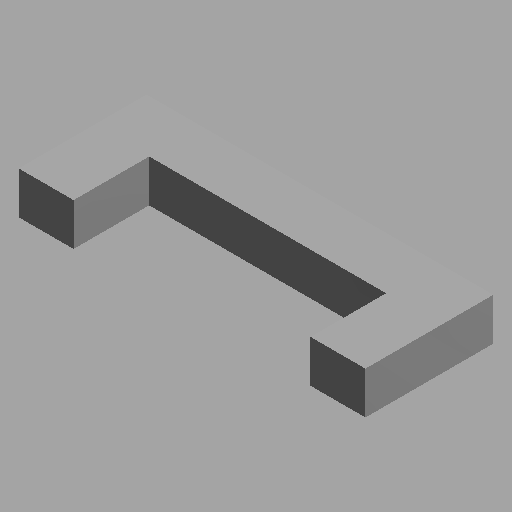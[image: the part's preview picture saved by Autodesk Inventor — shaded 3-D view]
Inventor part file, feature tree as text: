
AUTODESK INVENTOR PART (.ipt)
format: ipt  version: 2023 (Build 270158030, 158C)  size: 92,160 bytes
history: native  units: mm (DEFAULTED — no unit token found)
features: other x1, extrude x1, sketch x1
ambient origin geometry x8: Origin, YZ Plane, XZ Plane, XY Plane, X Axis, Y Axis, Z Axis, Center Point
bodies: Solid1 (feature_tree)
feature tree (3):
  other  "HBS"
  extrude  "Extrusion1"  Depth=227.0125mm
  sketch  "Sketch1"  dims[d0=711.2mm d1=227.0125mm d2=25.4mm d3=0.0mm]
